FCSTD DOCUMENT  (FreeCAD 0.21R33694 (Git))
Label: kumiko_assembly
License: All rights reserved
LicenseURL: http://en.wikipedia.org/wiki/All_rights_reserved
objects: App::Link×7, App::Part×2
EXTERNAL_REF file=../master_kumiko_box.FCStd obj=Spreadsheet
EXTERNAL_REF file=kumiko_lattice_assembly.FCStd obj=Part
EXTERNAL_REF file=asanoha_assembly.FCStd obj=Part001

FEATURE [App::Link] Link  label="SpreadSheet"
  LinkedObject = -> <external ../master_kumiko_box.FCStd>#Spreadsheet
FEATURE [App::Link] Link001  label="lattice"
  LinkedObject = -> <external kumiko_lattice_assembly.FCStd>#Part
FEATURE [App::Link] Link002  label="asanoha_left_bottom"
  LinkPlacement = pos=(3,3,0) rot=(0,0,1;0rad)
  LinkedObject = -> <external asanoha_assembly.FCStd>#Part001
  Placement = pos=(3,3,0) rot=(0,0,1;0rad)
  expr: .Placement.Base.x = <<SpreadSheet>>.kumiko_thickness
  expr: .Placement.Base.y = <<SpreadSheet>>.kumiko_thickness
FEATURE [App::Link] Link003  label="asanoha_left_top"
  LinkPlacement = pos=(3,55,0) rot=(0,0,1;4.71239rad)
  LinkedObject = -> <external asanoha_assembly.FCStd>#Part001
  Placement = pos=(3,55,0) rot=(0,0,1;4.71239rad)
  expr: .Placement.Base.x = <<SpreadSheet>>.kumiko_thickness
  expr: .Placement.Base.y = 2 * <<SpreadSheet>>.kumiko_grid_size
  expr: .Placement.Base.z = 0
FEATURE [App::Link] Link004  label="asanoha_right_bottom"
  LinkPlacement = pos=(55,3,0) rot=(0,0,1;1.5708rad)
  LinkedObject = -> Link002
  Placement = pos=(55,3,0) rot=(0,0,1;1.5708rad)
  expr: .Placement.Base.x = 2 * <<SpreadSheet>>.kumiko_grid_size
  expr: .Placement.Base.y = <<SpreadSheet>>.kumiko_thickness
FEATURE [App::Link] Link005  label="asanoha_right_top"
  LinkPlacement = pos=(30.5,30.5,0) rot=(0,0,1;0rad)
  LinkedObject = -> Link002
  Placement = pos=(30.5,30.5,0) rot=(0,0,1;0rad)
  expr: .Placement.Base.x = <<SpreadSheet>>.kumiko_grid_size + <<SpreadSheet>>.kumiko_thickness
  expr: .Placement.Base.y = <<SpreadSheet>>.kumiko_grid_size + <<SpreadSheet>>.kumiko_thickness
FEATURE [App::Part] Part  label="asanoha_left"
  Group = -> [Link004,Link005,Link003,Link002]
  Origin = -> Origin
FEATURE [App::Link] Link006  label="asanoha_right"
  LinkPlacement = pos=(55,0,0) rot=(0,0,1;0rad)
  LinkedObject = -> Part
  Placement = pos=(55,0,0) rot=(0,0,1;0rad)
  expr: .Placement.Base.x = 2 * <<SpreadSheet>>.kumiko_grid_size
FEATURE [App::Part] Part001  label="kumiko_assembly"
  Group = -> [Link006,Part,Link001]
  Origin = -> Origin001

RESOLVED EXTERNAL PARTS (link-assembly join: the EXTERNAL_REF files above that resolve inside this repo's crawl, each included once):
---- part ../master_kumiko_box.FCStd = doc fcstd_d57fc246fb5e ----
FCSTD DOCUMENT  (FreeCAD 0.21R33771 (Git))
Label: master_kumiko_box
License: All rights reserved
LicenseURL: https://en.wikipedia.org/wiki/All_rights_reserved
objects: App::Link×3, App::Part×2, Spreadsheet::Sheet×1
EXTERNAL_REF file=assembly/box_assembly.FCStd obj=Part
EXTERNAL_REF file=assembly/lid_assembly.FCStd obj=Part
EXTERNAL_REF file=assembly/kumiko_assembly.FCStd obj=Part001

FEATURE [Spreadsheet::Sheet] Spreadsheet  label="SpreadSheet"
  cells = A1='name; B1='value; C1='calc (y/n); A2='box_length; B2(box_length)=130; C2='n; A3='box_width; B3(box_width)==B2 / 2 + B5 - B13 / 2; C3='n; A4='box_height; B4(box_height)=60; C4='y; A5='box_thickness; B5(box_thickness)=11.5; C5='y; A7='lid_height; B7(lid_height)==B8 * 17 / 8.5; C7='y; A8='lid_frame_width; B8(lid_frame_width)==B5 - B13; C8='y; A9='lid_lip_width; B9(lid_lip_width)==B5 - B8; C9='y; A10='lid_lip_height; B10(lid_lip_hight)=3; C10='y; A12='kumiko_hight; B12(kumiko_hight)==B7 * 11 / 17; C12='y; A13='kumiko_thickness; B13(kumiko_thickness)=3; C13='n; A14='kumiko_grid_size; B14(kumiko_grid_size)==(B2 - 2 * B8 - B13) / 4; C14='y; A16='box_wall_height; B16(box_wall_height)==B4 - B7 - B18; C16='y; A18='floor_edge; B18(floor_edge)=2; C18='n; A20='cnc_spacing; B20(cnc_spacing)=0; C20='y
FEATURE [App::Link] Link  label="box"
  LinkedObject = -> <external assembly/box_assembly.FCStd>#Part
FEATURE [App::Link] Link001  label="lid"
  LinkPlacement = pos=(0,0,43) rot=(0,0,1;0rad)
  LinkedObject = -> <external assembly/lid_assembly.FCStd>#Part
  Placement = pos=(0,0,43) rot=(0,0,1;0rad)
  expr: .Placement.Base.z = <<SpreadSheet>>.box_height - <<SpreadSheet>>.lid_height
FEATURE [App::Link] Link002  label="kumiko_assembly"
  LinkPlacement = pos=(8.5,8.5,49) rot=(0,0,1;0rad)
  LinkedObject = -> <external assembly/kumiko_assembly.FCStd>#Part001
  Placement = pos=(8.5,8.5,49) rot=(0,0,1;0rad)
  expr: .Placement.Base.x = <<SpreadSheet>>.lid_frame_width
  expr: .Placement.Base.y = <<SpreadSheet>>.lid_frame_width
  expr: .Placement.Base.z = <<SpreadSheet>>.box_height - Spreadsheet.kumiko_hight
FEATURE [App::Part] Part  label="lid_complete"
  Group = -> [Link002,Link001]
  Origin = -> Origin
FEATURE [App::Part] Part001  label="kumiko_box_complete"
  Group = -> [Part,Link]
  Origin = -> Origin001
---- part asanoha_assembly.FCStd = doc fcstd_f89c38ed9356 ----
FCSTD DOCUMENT  (FreeCAD 0.21R33694 (Git))
Label: asanoha_assembly
License: All rights reserved
LicenseURL: http://en.wikipedia.org/wiki/All_rights_reserved
objects: App::Link×6, App::Part×2
EXTERNAL_REF file=../master_kumiko_box.FCStd obj=Spreadsheet
EXTERNAL_REF file=../parts/kumiko/kumiko_inlay_diagonal.FCStd obj=Body063
EXTERNAL_REF file=../parts/kumiko/kumiko_inlay_hindge.FCStd obj=Body062
EXTERNAL_REF file=../parts/kumiko/kumiko_inlay_short_diagonal.FCStd obj=Body064

FEATURE [App::Link] Link  label="SpreadSheet"
  LinkedObject = -> <external ../master_kumiko_box.FCStd>#Spreadsheet
FEATURE [App::Link] Link001  label="long_diagonal"
  LinkedObject = -> <external ../parts/kumiko/kumiko_inlay_diagonal.FCStd>#Body063
FEATURE [App::Link] Link004  label="hindge_body001"
  LinkPlacement = pos=(2.12132,0,11) rot=(1,1,0;3.14159rad)
  LinkedObject = -> <external ../parts/kumiko/kumiko_inlay_hindge.FCStd>#Body062
  Placement = pos=(2.12132,0,11) rot=(1,1,0;3.14159rad)
  expr: .Placement.Base.x = <<SpreadSheet>>.kumiko_thickness / sqrt(2)
  expr: .Placement.Base.y = 0
  expr: .Placement.Base.z = <<SpreadSheet>>.kumiko_hight
FEATURE [App::Link] Link005  label="short_diagonal001"
  LinkPlacement = pos=(24.5,0,0) rot=(0,0,1;3.14159rad)
  LinkedObject = -> <external ../parts/kumiko/kumiko_inlay_short_diagonal.FCStd>#Body064
  Placement = pos=(24.5,0,0) rot=(0,0,1;3.14159rad)
  expr: .Placement.Base.x = <<SpreadSheet>>.kumiko_grid_size - <<SpreadSheet>>.kumiko_thickness
FEATURE [App::Link] Link006  label="hindge_body002"
  LinkPlacement = pos=(24.5,22.3787,0) rot=(0,0,1;3.14159rad)
  LinkedObject = -> <external ../parts/kumiko/kumiko_inlay_hindge.FCStd>#Body062
  Placement = pos=(24.5,22.3787,0) rot=(0,0,1;3.14159rad)
  expr: .Placement.Base.x = <<SpreadSheet>>.kumiko_grid_size - <<SpreadSheet>>.kumiko_thickness
  expr: .Placement.Base.y = <<SpreadSheet>>.kumiko_grid_size - <<SpreadSheet>>.kumiko_thickness - <<SpreadSheet>>.kumiko_thickness / sqrt(2)
FEATURE [App::Part] Part  label="inlay_top_left"
  Group = -> [Link006,Link005,Link004]
  Origin = -> Origin
  Placement = pos=(0,0,11) rot=(1,1,0;3.14159rad)
  expr: .Placement.Base.z = <<SpreadSheet>>.kumiko_hight
FEATURE [App::Link] Link007  label="inlay_bottom_right"
  LinkedObject = -> Part
FEATURE [App::Part] Part001  label="asanoha"
  Group = -> [Link007,Part,Link001]
  Origin = -> Origin001
---- part kumiko_lattice_assembly.FCStd = doc fcstd_7906d9c5b7b7 ----
FCSTD DOCUMENT  (FreeCAD 0.21R33694 (Git))
Label: kumiko_lattice_assembly
License: All rights reserved
LicenseURL: http://en.wikipedia.org/wiki/All_rights_reserved
objects: App::Link×9, App::Part×1
EXTERNAL_REF file=../master_kumiko_box.FCStd obj=Spreadsheet
EXTERNAL_REF file=../parts/kumiko/kumiko_strip_short.FCStd obj=Body052
EXTERNAL_REF file=../parts/kumiko/kumiko_strip_long.FCStd obj=Body053
EXTERNAL_REF file=../parts/kumiko/kumiko_strip_long_holes.FCStd obj=Body052
EXTERNAL_REF file=../parts/kumiko/kumiko_strip_short_holes.FCStd obj=Body052

FEATURE [App::Link] Link002  label="SpreadSheet"
  LinkedObject = -> <external ../master_kumiko_box.FCStd>#Spreadsheet
FEATURE [App::Link] Link003  label="short_strip_a"
  LinkPlacement = pos=(27.5,3,11) rot=(1,1,0;3.14159rad)
  LinkedObject = -> <external ../parts/kumiko/kumiko_strip_short.FCStd>#Body052
  Placement = pos=(27.5,3,11) rot=(1,1,0;3.14159rad)
  expr: .Placement.Base.x = <<SpreadSheet>>.kumiko_grid_size
  expr: .Placement.Base.y = <<SpreadSheet>>.kumiko_thickness
  expr: .Placement.Base.z = <<SpreadSheet>>.kumiko_hight
  expr: .Placement.Rotation.Angle = 180
  expr: .Placement.Rotation.Axis.x = 1
  expr: .Placement.Rotation.Axis.y = 1
  expr: .Placement.Rotation.Axis.z = 0
FEATURE [App::Link] Link004  label="short_strip_b"
  LinkPlacement = pos=(55,3,11) rot=(1,1,0;3.14159rad)
  LinkedObject = -> <external ../parts/kumiko/kumiko_strip_short.FCStd>#Body052
  Placement = pos=(55,3,11) rot=(1,1,0;3.14159rad)
  expr: .Placement.Base.x = <<SpreadSheet>>.kumiko_grid_size * 2
  expr: .Placement.Base.y = <<SpreadSheet>>.kumiko_thickness
  expr: .Placement.Base.z = <<SpreadSheet>>.kumiko_hight
  expr: .Placement.Rotation.Angle = 180
  expr: .Placement.Rotation.Axis.x = 1
  expr: .Placement.Rotation.Axis.y = 1
  expr: .Placement.Rotation.Axis.z = 0
FEATURE [App::Link] Link005  label="short_strip_c"
  LinkPlacement = pos=(82.5,3,11) rot=(1,1,0;3.14159rad)
  LinkedObject = -> <external ../parts/kumiko/kumiko_strip_short.FCStd>#Body052
  Placement = pos=(82.5,3,11) rot=(1,1,0;3.14159rad)
  expr: .Placement.Base.x = <<SpreadSheet>>.kumiko_grid_size * 3
  expr: .Placement.Base.y = <<SpreadSheet>>.kumiko_thickness
  expr: .Placement.Base.z = <<SpreadSheet>>.kumiko_hight
  expr: .Placement.Rotation.Angle = 180
  expr: .Placement.Rotation.Axis.x = 1
  expr: .Placement.Rotation.Axis.y = 1
  expr: .Placement.Rotation.Axis.z = 0
FEATURE [App::Link] Link009  label="strip_long_center"
  LinkPlacement = pos=(3,27.5,0) rot=(0,0,1;0rad)
  LinkedObject = -> <external ../parts/kumiko/kumiko_strip_long.FCStd>#Body053
  Placement = pos=(3,27.5,0) rot=(0,0,1;0rad)
  expr: .Placement.Base.x = <<SpreadSheet>>.kumiko_thickness
  expr: .Placement.Base.y = <<SpreadSheet>>.kumiko_grid_size
FEATURE [App::Link] Link  label="strip_long_front"
  LinkPlacement = pos=(3,0,0) rot=(0,0,1;0rad)
  LinkedObject = -> <external ../parts/kumiko/kumiko_strip_long_holes.FCStd>#Body052
  Placement = pos=(3,0,0) rot=(0,0,1;0rad)
  expr: .Placement.Base.x = <<SpreadSheet>>.kumiko_thickness
FEATURE [App::Link] Link010  label="strip_long_back"
  LinkPlacement = pos=(3,55,0) rot=(0,0,1;0rad)
  LinkedObject = -> <external ../parts/kumiko/kumiko_strip_long_holes.FCStd>#Body052
  Placement = pos=(3,55,0) rot=(0,0,1;0rad)
  expr: .Placement.Base.x = <<SpreadSheet>>.kumiko_thickness
  expr: .Placement.Base.y = <<SpreadSheet>>.kumiko_grid_size * 2
FEATURE [App::Link] Link011  label="short_strip_left"
  LinkPlacement = pos=(0,0,11) rot=(1,1,0;3.14159rad)
  LinkedObject = -> <external ../parts/kumiko/kumiko_strip_short_holes.FCStd>#Body052
  Placement = pos=(0,0,11) rot=(1,1,0;3.14159rad)
  expr: .Placement.Base.y = 0
  expr: .Placement.Base.z = <<SpreadSheet>>.kumiko_hight
FEATURE [App::Link] Link012  label="short_strip_right"
  LinkPlacement = pos=(110,0,11) rot=(1,1,0;3.14159rad)
  LinkedObject = -> <external ../parts/kumiko/kumiko_strip_short_holes.FCStd>#Body052
  Placement = pos=(110,0,11) rot=(1,1,0;3.14159rad)
  expr: .Placement.Base.x = <<SpreadSheet>>.kumiko_grid_size * 4
  expr: .Placement.Base.y = 0
  expr: .Placement.Base.z = <<SpreadSheet>>.kumiko_hight
FEATURE [App::Part] Part  label="lattice"
  Group = -> [Link005,Link,Link003,Link009,Link004,Link010,Link011,Link012]
  Origin = -> Origin
